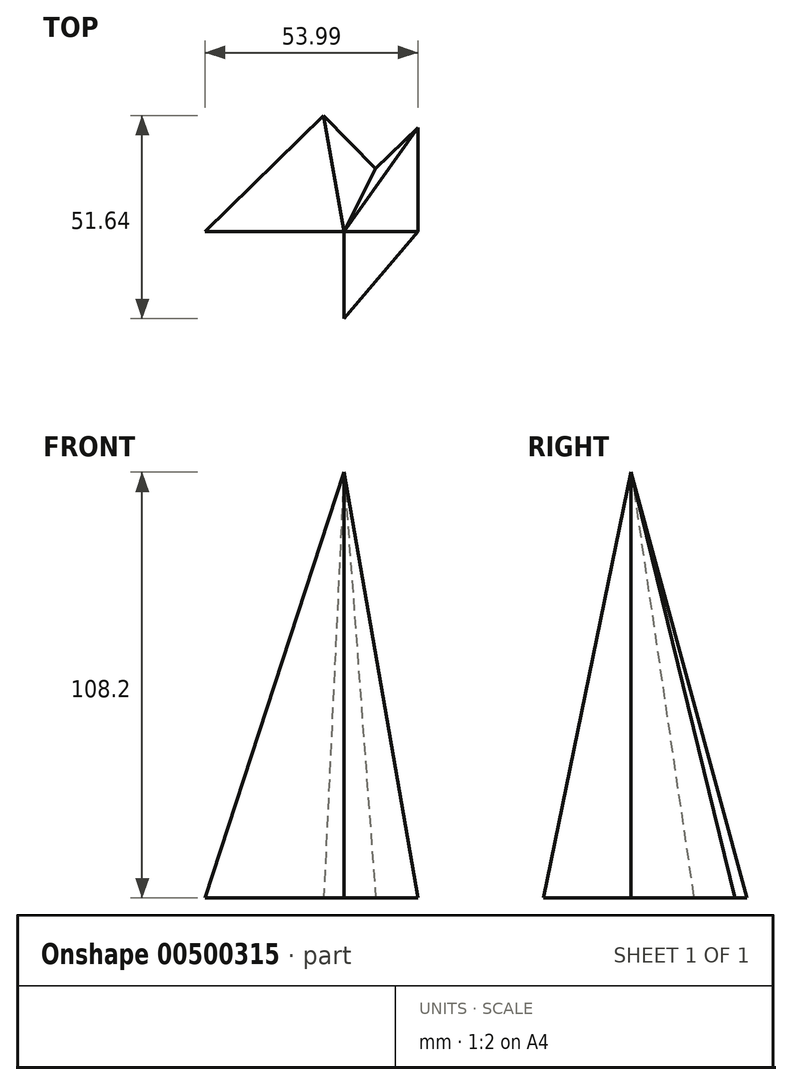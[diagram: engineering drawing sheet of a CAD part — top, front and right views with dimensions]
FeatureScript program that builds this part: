
annotation { "Feature Type Name" : "Feature", "Feature Type Description" : "" }
export const myFeature = defineFeature(function(context is Context, id is Id, definition is map)
    precondition{}
    {
        {
            var Q0;
            Q0=qCreatedBy(makeId("Top.planeOp"),FACE);
            var sketch = newSketch(context, id + "F0", { "sketchPlane" : qUnion([Q0])});
            skLineSegment(sketch, "E0", {"start": v(-35.22, 0) * mm, "end": v(-5.13, 29.44) * mm});
            skLineSegment(sketch, "E1", {"start": v(-5.13, 29.44) * mm, "end": v(8.07, 15.95) * mm});
            skLineSegment(sketch, "E2", {"start": v(8.07, 15.95) * mm, "end": v(18.77, 26.41) * mm});
            skLineSegment(sketch, "E3", {"start": v(18.77, 26.41) * mm, "end": v(18.77, 0) * mm});
            skLineSegment(sketch, "E4", {"start": v(18.77, 0) * mm, "end": v(0, -22.2) * mm});
            skLineSegment(sketch, "E5", {"start": v(0, -22.2) * mm, "end": v(0, 0) * mm});
            skLineSegment(sketch, "E6", {"start": v(0, 0) * mm, "end": v(-35.22, 0) * mm});
            skSolve(sketch);
        }
        {
            var Q0;
            Q0=qCreatedBy(makeId("Top.planeOp"),FACE);
            cPlane(context, id + "F1", {"entities" : qUnion([Q0]), "cplaneType" : CPlaneType.OFFSET, "offset" : 108.2 * mm, "width" : 152.4 * mm, "height" : 152.4 * mm});
        }
        {
            var Q0;
            Q0=qCreatedBy(id+"F1.planeOp",FACE);
            var sketch = newSketch(context, id + "F2", { "sketchPlane" : qUnion([Q0])});
            skPoint(sketch, "E7", {"position": v(0, 0) * mm});
            skSolve(sketch);
        }
        {
            var Q0;
            Q0=sQuery(id+"F2.wireOp",VERTEX,"E7");
            var Q1;
            Q1=makeQuery(id+"F0.imprint","IMPRINT",FACE,{"disambiguationData":[TD([[makeQuery(id+"F0.imprint","IMPRINT",EDGE,{"derivedFrom":sQuery(id+"F0.wireOp",EDGE,"E0")}),-1.0]])]});
            loft(context, id + "F3", {"sheetProfilesArray" : [{ "sheetProfileEntities" : qUnion([Q0]) }, { "sheetProfileEntities" : qUnion([Q1]) }]});
        }
    });
